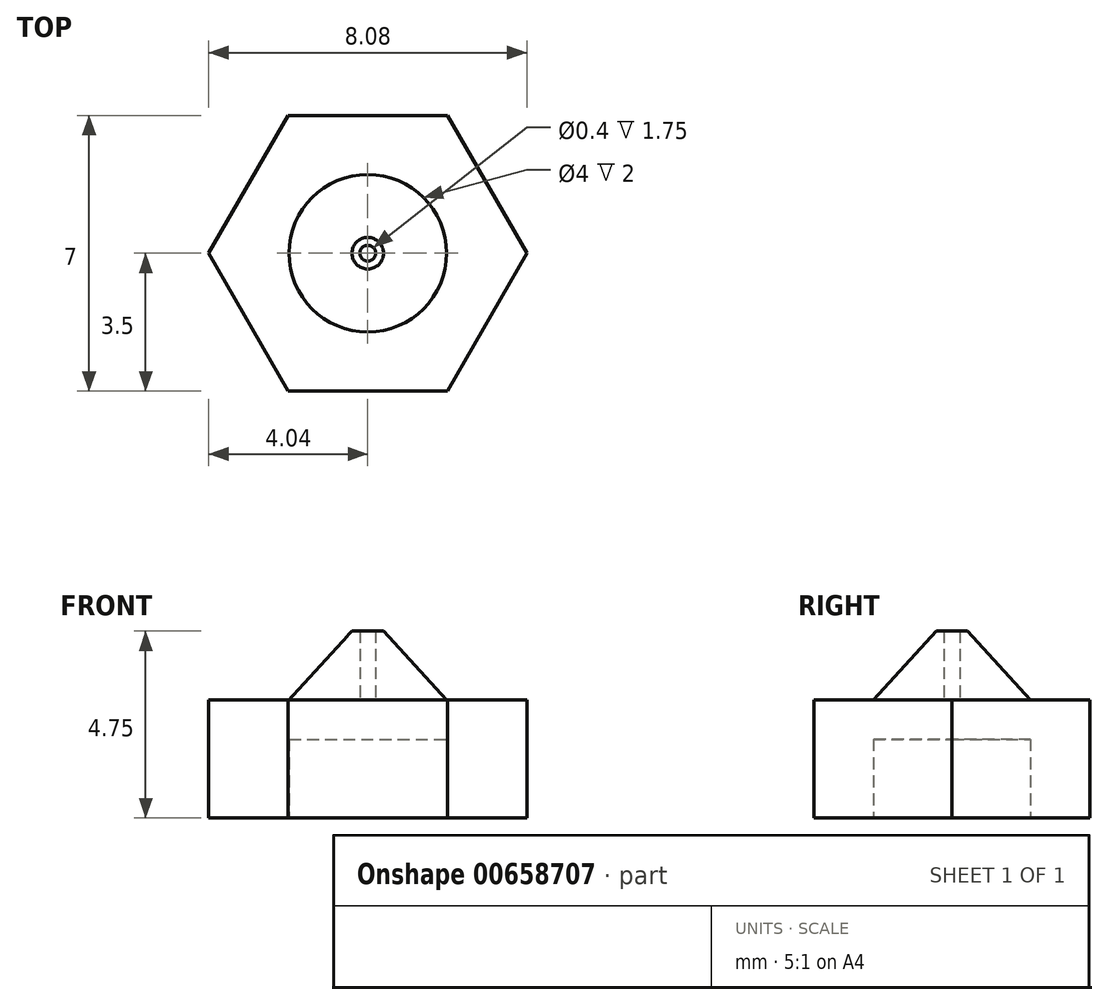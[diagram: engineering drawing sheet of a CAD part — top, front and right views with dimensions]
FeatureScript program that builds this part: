
annotation { "Feature Type Name" : "Feature", "Feature Type Description" : "" }
export const myFeature = defineFeature(function(context is Context, id is Id, definition is map)
    precondition{}
    {
        {
            var Q0;
            Q0=qCreatedBy(makeId("Top.planeOp"),FACE);
            var sketch = newSketch(context, id + "F0", { "sketchPlane" : qUnion([Q0])});
            skCircle(sketch, "E0.cCircle", {"center": v(0, 0) * mm, "radius": 4.04 * mm, "construction": true});
            skLineSegment(sketch, "E0.0", {"start": v(4.04, 0) * mm, "end": v(2.02, -3.5) * mm});
            skLineSegment(sketch, "E0.1", {"start": v(2.02, -3.5) * mm, "end": v(-2.02, -3.5) * mm});
            skLineSegment(sketch, "E0.2", {"start": v(-2.02, -3.5) * mm, "end": v(-4.04, 0) * mm});
            skLineSegment(sketch, "E0.3", {"start": v(-4.04, 0) * mm, "end": v(-2.02, 3.5) * mm});
            skLineSegment(sketch, "E0.4", {"start": v(-2.02, 3.5) * mm, "end": v(2.02, 3.5) * mm});
            skLineSegment(sketch, "E0.5", {"start": v(2.02, 3.5) * mm, "end": v(4.04, 0) * mm});
            skSolve(sketch);
        }
        {
            var Q0;
            Q0=makeQuery(id+"F0.imprint","IMPRINT",FACE,{"disambiguationData":[TD([[makeQuery(id+"F0.imprint","IMPRINT",EDGE,{"derivedFrom":sQuery(id+"F0.wireOp",EDGE,"E0.0")}),-1.0]])]});
            extrude(context, id + "F1", {"entities" : qUnion([Q0]), "depth" : 3 * mm});
        }
        {
            var Q0;
            Q0=qCreatedBy(makeId("Right.planeOp"),FACE);
            var sketch = newSketch(context, id + "F2", { "sketchPlane" : qUnion([Q0])});
            skLineSegment(sketch, "E1.0", {"start": v(-3.5, 3) * mm, "end": v(0, 3) * mm});
            skLineSegment(sketch, "E2.0", {"start": v(0, 3) * mm, "end": v(3.5, 3) * mm});
            skLineSegment(sketch, "E3", {"start": v(-0.2, 3) * mm, "end": v(-0.2, 4.75) * mm});
            skLineSegment(sketch, "E4", {"start": v(-0.2, 4.75) * mm, "end": v(-0.4, 4.75) * mm});
            skLineSegment(sketch, "E5", {"start": v(-0.4, 4.75) * mm, "end": v(-2, 3) * mm});
            skLineSegment(sketch, "E6", {"start": v(-2, 3) * mm, "end": v(-0.2, 3) * mm});
            skLineSegment(sketch, "E7", {"start": v(0, 3) * mm, "end": v(0, 3.62) * mm});
            skSolve(sketch);
        }
        {
            var Q0;
            Q0=makeQuery(id+"F2.imprint","IMPRINT",FACE,{"disambiguationData":[TD([[makeQuery(id+"F2.imprint","IMPRINT",EDGE,{"derivedFrom":sQuery(id+"F2.wireOp",EDGE,"E3")}),1.0]])]});
            var Q1;
            Q1=sQuery(id+"F2.wireOp",EDGE,"E7");
            revolve(context, id + "F3", {"operationType" : NewBodyOperationType.ADD, "entities" : qUnion([Q0]), "axis" : qUnion([Q1]), "revolveType" : RevolveType.FULL});
        }
        {
            var Q0;
            Q0=makeQuery(id+"F1.opExtrude","CAP_FACE",FACE,{"disambiguationData":[OSD([sQuery(id+"F0.wireOp",EDGE,"E0.0"),sQuery(id+"F0.wireOp",EDGE,"E0.1"),sQuery(id+"F0.wireOp",EDGE,"E0.2"),sQuery(id+"F0.wireOp",EDGE,"E0.3"),sQuery(id+"F0.wireOp",EDGE,"E0.4"),sQuery(id+"F0.wireOp",EDGE,"E0.5")])],"isStart":true});
            var sketch = newSketch(context, id + "F4", { "sketchPlane" : qUnion([Q0])});
            skCircle(sketch, "E8", {"center": v(0, 0) * mm, "radius": 2 * mm});
            skSolve(sketch);
        }
        {
            var Q0;
            Q0=makeQuery(id+"F4.imprint","IMPRINT",FACE,{"disambiguationData":[TD([[makeQuery(id+"F4.imprint","IMPRINT",EDGE,{"derivedFrom":sQuery(id+"F4.wireOp",EDGE,"E8")}),1.0]])]});
            extrude(context, id + "F5", {"entities" : qUnion([Q0]), "operationType" : NewBodyOperationType.REMOVE, "oppositeDirection" : true, "depth" : 2 * mm});
        }
    });
